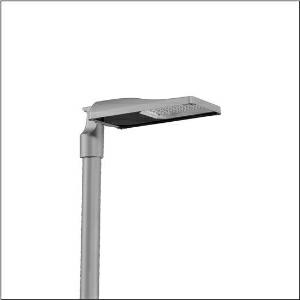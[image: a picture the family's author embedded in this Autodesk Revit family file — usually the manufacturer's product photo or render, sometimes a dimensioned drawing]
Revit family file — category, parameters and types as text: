
# Revit family: streetlight_sl_31_mini___st1_0a_5xh6d3aa08ha_c65b
name_source: partatom
category: Lighting Fixtures
units: mm (PartAtom-declared; Revit-internal decimal feet)

## family parameters
Cut with Voids When Loaded = No
Host = Face
Light Source = No
Part Type = Normal
Room Calculation Point = No
Round Connector Dimension = Use Diameter
Shared = No

## types (1)
- --- (1 x LED, 9240 lm, 68.3 W, 3000K)
    Apparent Load = 68 VA
    CIE Flux Codes = 37 72 97 100 100
    Color Rendering = 70
    Color Temperature = 3000K
    Default Elevation = 1800 mm
    Description = Streetlight SL 31 mini Easy mast luminaire for post-top, side-entry; light control with lens of PMMA; light distribution: ST1.0a, direct asymmetric distribution, for standard-compliant lighting for roads and squares; LED: luminous flux: 9.240lm, light colour: 730, colour temperature: 3000K; luminous efficacy: 135,3lm/W; control: pre-setting: linear dimming characteristic, flexible luminous flux parameterisation, time-dependent luminous flux control, constant luminous flux control, intelligent temperature release in ECG and LED module, overheat protection; luminaire housing, of diecast aluminium, SITECO metallic grey (DB 702S), corrosivity category C5 high according to DIN EN ISO 12944; cover of toughened safety glass, transparent, opened without tools; mast flange of diecast aluminium, SITECO metallic grey (DB 702S), spigot size: 76/60mm, mast flange included unmounted; cable length: 8,5m, connection cable pre-assembled; mains connection: 220..240V, AC, 50/60Hz; power consumption (at start of service life): 68,3W / (at end of service life): 74,8W / (with reduced operation 50%): 29,7W; protection rating (complete): IP66; insulation class (complete): insulation class II (safety insulation); impact resistance: IK10; certification: CE, ENEC, ENEC+, VDE, UKCA; permissible operating ambient temperature for outdoor applications: -40..+50°C; packaging unit: 1 piece

Light Distribution: ST1.0a
    Height = 76 mm
    Lamp = 1 x LED
    Lamp Light Flux = 9240 lm
    Lamp Power = 68.3 W
    Lamp count = 1
    Length = 547 mm
    Luminous efficacy = 135 lm/W
    Manufacturer = Siteco
    ModVariant = No
    Model = 5XH6D3AA08HA
    Number of Poles = 1
    OnlyDefault = Yes
    Power Factor = 1
    Product Name = Streetlight SL 31 mini | ST1.0a
    Product group = mast luminaire | pylon top
    ProductGroupID = 6100
    Protection Class = Protection class II
    Protection Degree = IP 66
    RLX_Detail_Level = 1
    RLX_Emergency_Light_Flux = 0 lm
    RLX_Emergency_Type = 0
    RLX_Emergency_Type_DB = No
    RlxData = <blob elided: 39341 chars, md5=4c584363>
    Socket = socket
    Standby Power = 0 W
    System Light Flux = 9240 lm
    System Power = 68 W
    Type Comments = factory setting: luminous flux: 100 % | dim-lin: 254 | 693 mA
    Type Image = l_1300326.jpg
    URL = http://relux.com
    VarID = @adj_060981
    Voltage = 0 V
    Weight = 0.00 kg
    Width = 265 mm

## geometry (parser evidence)
native form markers: Blend x4, Sweep x8
no freeform markers — native parametric forms only
